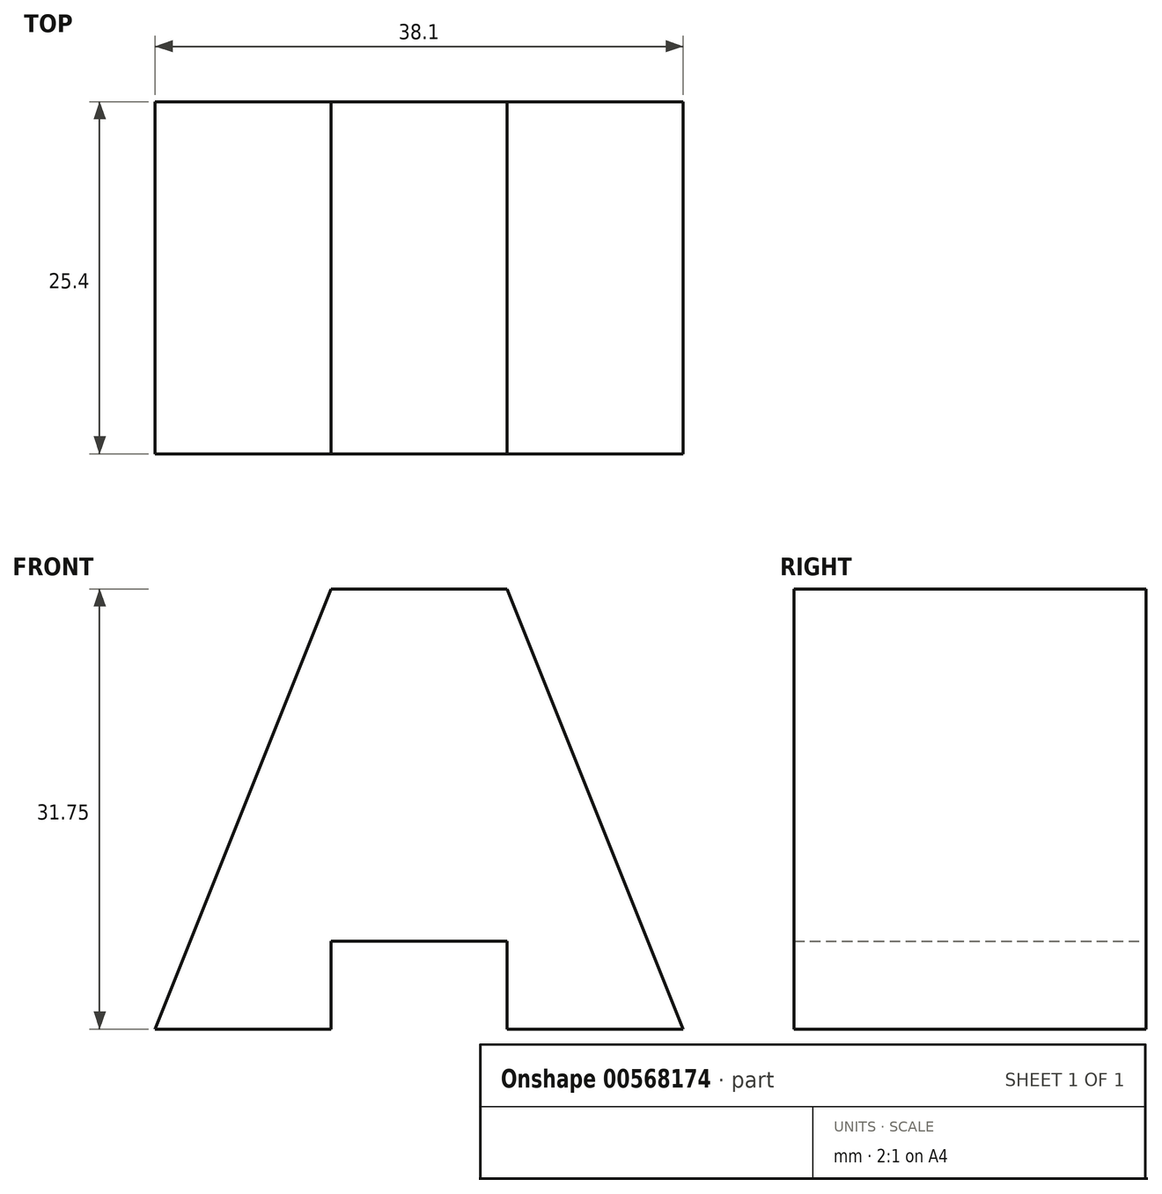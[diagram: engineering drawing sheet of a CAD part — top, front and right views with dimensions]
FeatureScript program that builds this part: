
annotation { "Feature Type Name" : "Feature", "Feature Type Description" : "" }
export const myFeature = defineFeature(function(context is Context, id is Id, definition is map)
    precondition{}
    {
        {
            var Q0;
            Q0=qCreatedBy(makeId("Front.planeOp"),FACE);
            var sketch = newSketch(context, id + "F0", { "sketchPlane" : qUnion([Q0])});
            skLineSegment(sketch, "E0", {"start": v(-49.27, 47.79) * mm, "end": v(-36.57, 47.79) * mm});
            skLineSegment(sketch, "E1", {"start": v(-49.27, 47.79) * mm, "end": v(-61.97, 16.04) * mm});
            skLineSegment(sketch, "E2", {"start": v(-36.57, 47.79) * mm, "end": v(-23.87, 16.04) * mm});
            skLineSegment(sketch, "E3", {"start": v(-23.87, 16.04) * mm, "end": v(-36.57, 16.04) * mm});
            skLineSegment(sketch, "E4", {"start": v(-61.97, 16.04) * mm, "end": v(-49.27, 16.04) * mm});
            skLineSegment(sketch, "E5", {"start": v(-36.57, 16.04) * mm, "end": v(-36.57, 22.39) * mm});
            skLineSegment(sketch, "E6", {"start": v(-49.27, 16.04) * mm, "end": v(-49.27, 22.39) * mm});
            skLineSegment(sketch, "E7", {"start": v(-49.27, 22.39) * mm, "end": v(-36.57, 22.39) * mm});
            skSolve(sketch);
        }
        {
            var Q0;
            Q0 = qSketchRegion(id + "F0", true);
            extrude(context, id + "F1", {"entities" : qUnion([Q0]), "depth" : 25.4 * mm, "offsetDistance" : 25.4 * mm});
        }
    });
